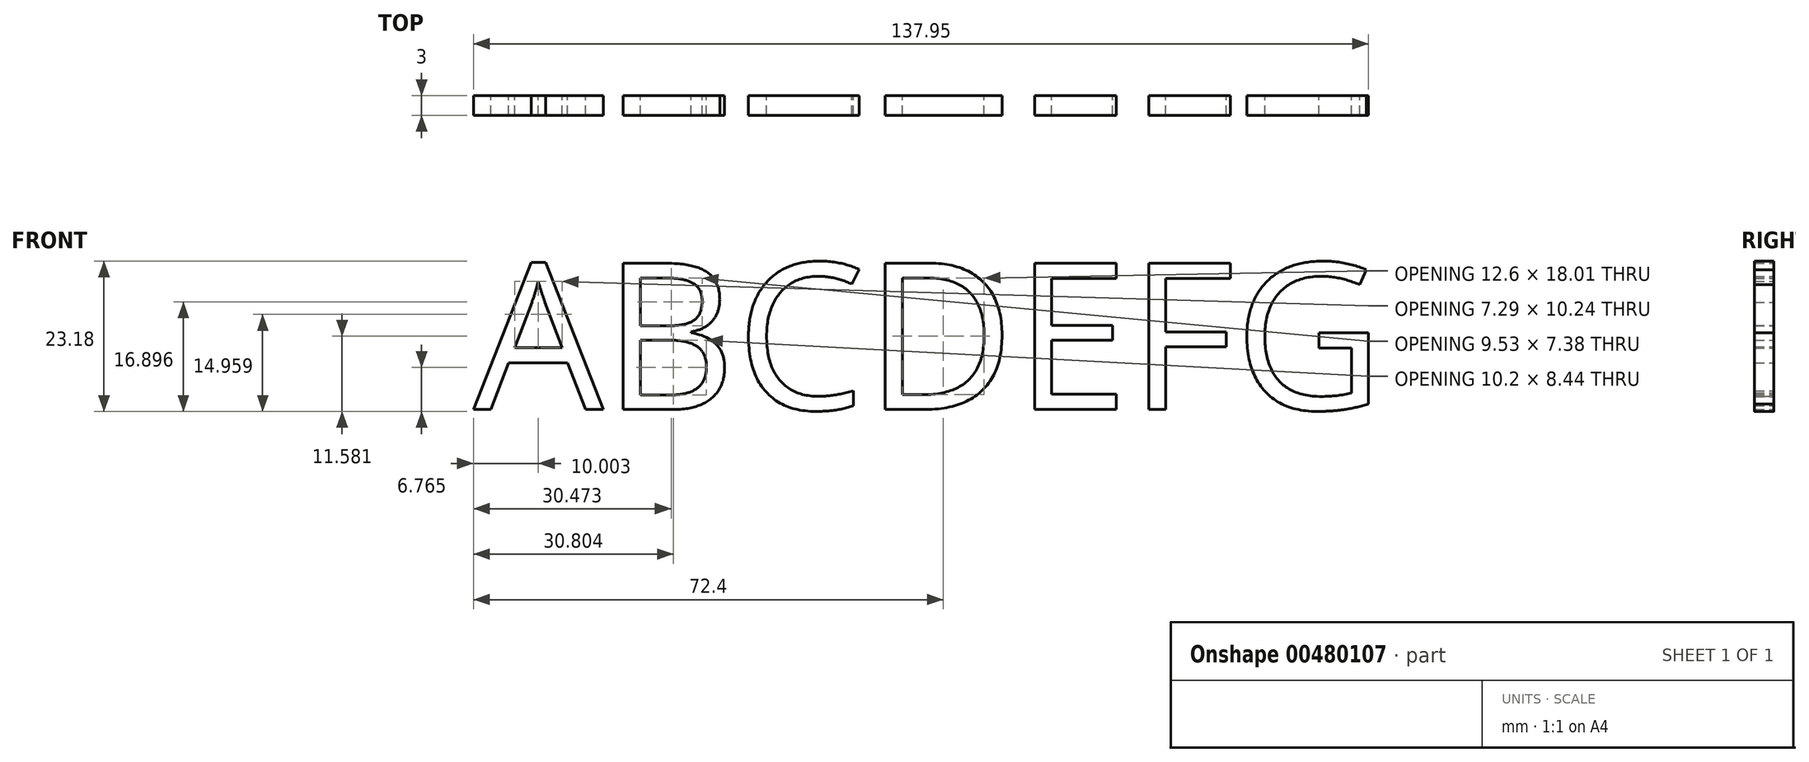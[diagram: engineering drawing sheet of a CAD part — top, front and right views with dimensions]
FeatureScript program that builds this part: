
annotation { "Feature Type Name" : "Feature", "Feature Type Description" : "" }
export const myFeature = defineFeature(function(context is Context, id is Id, definition is map)
    precondition{}
    {
        {
            var Q0;
            Q0=qCreatedBy(makeId("Front.planeOp"),FACE);
            var sketch = newSketch(context, id + "F0", { "sketchPlane" : qUnion([Q0])});
            skText(sketch, "E0", { "text": "ABCDEFG", "fontName": "OpenSans-Regular.ttf"});
            const initialGuessF0  = {"E0": [-0.0709, -0.01017, 1, 0, 0.02274]};
            skSetInitialGuess(sketch, initialGuessF0);
            skSolve(sketch);
        }
        {
            var Q0;
            Q0=makeQuery(id+"F0.imprint","IMPRINT",FACE,{"disambiguationData":[TD([[makeQuery(id+"F0.imprint","IMPRINT",EDGE,{"derivedFrom":sQuery(id+"F0.wireOp",EDGE,"E0.sketch_text.stroke-13")}),-1.0]])]});
            var Q1;
            Q1=makeQuery(id+"F0.imprint","IMPRINT",FACE,{"disambiguationData":[TD([[makeQuery(id+"F0.imprint","IMPRINT",EDGE,{"derivedFrom":sQuery(id+"F0.wireOp",EDGE,"E0.sketch_text.stroke-0")}),-1.0]])]});
            var Q2;
            Q2=makeQuery(id+"F0.imprint","IMPRINT",FACE,{"disambiguationData":[TD([[makeQuery(id+"F0.imprint","IMPRINT",EDGE,{"derivedFrom":sQuery(id+"F0.wireOp",EDGE,"E0.sketch_text.stroke-38")}),-1.0]])]});
            var Q3;
            Q3=makeQuery(id+"F0.imprint","IMPRINT",FACE,{"disambiguationData":[TD([[makeQuery(id+"F0.imprint","IMPRINT",EDGE,{"derivedFrom":sQuery(id+"F0.wireOp",EDGE,"E0.sketch_text.stroke-53")}),-1.0]])]});
            var Q4;
            Q4=makeQuery(id+"F0.imprint","IMPRINT",FACE,{"disambiguationData":[TD([[makeQuery(id+"F0.imprint","IMPRINT",EDGE,{"derivedFrom":sQuery(id+"F0.wireOp",EDGE,"E0.sketch_text.stroke-67")}),-1.0]])]});
            var Q5;
            Q5=makeQuery(id+"F0.imprint","IMPRINT",FACE,{"disambiguationData":[TD([[makeQuery(id+"F0.imprint","IMPRINT",EDGE,{"derivedFrom":sQuery(id+"F0.wireOp",EDGE,"E0.sketch_text.stroke-79")}),-1.0]])]});
            var Q6;
            Q6=makeQuery(id+"F0.imprint","IMPRINT",FACE,{"disambiguationData":[TD([[makeQuery(id+"F0.imprint","IMPRINT",EDGE,{"derivedFrom":sQuery(id+"F0.wireOp",EDGE,"E0.sketch_text.stroke-89")}),-1.0]])]});
            extrude(context, id + "F1", {"entities" : qUnion([Q0, Q1, Q2, Q3, Q4, Q5, Q6]), "depth" : 3 * mm});
        }
    });
